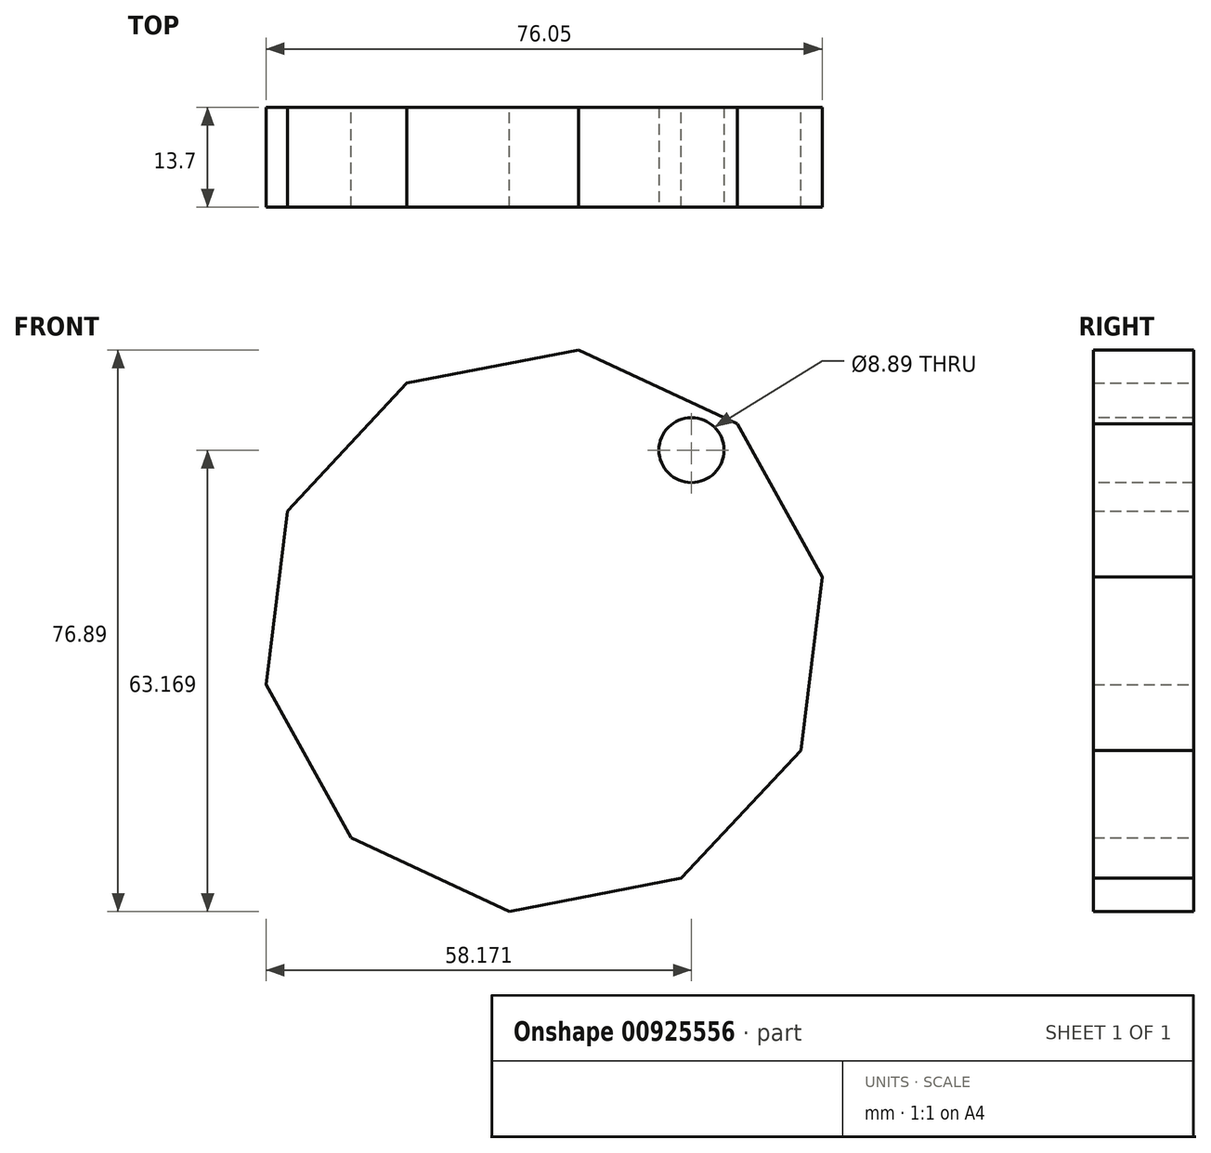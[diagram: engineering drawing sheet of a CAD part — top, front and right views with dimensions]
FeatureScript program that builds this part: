
annotation { "Feature Type Name" : "Feature", "Feature Type Description" : "" }
export const myFeature = defineFeature(function(context is Context, id is Id, definition is map)
    precondition{}
    {
        {
            var Q0;
            Q0=qCreatedBy(makeId("Front.planeOp"),FACE);
            var sketch = newSketch(context, id + "F0", { "sketchPlane" : qUnion([Q0])});
            skCircle(sketch, "E0.cCircle", {"center": v(-8.58, 14.77) * mm, "radius": 38.73 * mm, "construction": true});
            skLineSegment(sketch, "E0.0", {"start": v(10.19, -19.12) * mm, "end": v(-13.31, -23.68) * mm});
            skLineSegment(sketch, "E0.1", {"start": v(-13.31, -23.68) * mm, "end": v(-35, -13.56) * mm});
            skLineSegment(sketch, "E0.2", {"start": v(-35, -13.56) * mm, "end": v(-46.6, 7.38) * mm});
            skLineSegment(sketch, "E0.3", {"start": v(-46.6, 7.38) * mm, "end": v(-43.69, 31.14) * mm});
            skLineSegment(sketch, "E0.4", {"start": v(-43.69, 31.14) * mm, "end": v(-27.36, 48.65) * mm});
            skLineSegment(sketch, "E0.5", {"start": v(-27.36, 48.65) * mm, "end": v(-3.86, 53.2) * mm});
            skLineSegment(sketch, "E0.6", {"start": v(-3.86, 53.2) * mm, "end": v(17.84, 43.09) * mm});
            skLineSegment(sketch, "E0.7", {"start": v(17.84, 43.09) * mm, "end": v(29.44, 22.15) * mm});
            skLineSegment(sketch, "E0.8", {"start": v(29.44, 22.15) * mm, "end": v(26.52, -1.61) * mm});
            skLineSegment(sketch, "E0.9", {"start": v(26.52, -1.61) * mm, "end": v(10.19, -19.12) * mm});
            skSolve(sketch);
        }
        {
            var Q0;
            Q0 = qSketchRegion(id + "F0", true);
            extrude(context, id + "F1", {"entities" : qUnion([Q0]), "depth" : 13.7 * mm, "offsetDistance" : 25 * mm});
        }
        {
            var Q0;
            Q0=makeQuery(id+"F1.opExtrude","CAP_FACE",FACE,{"disambiguationData":[OSD([sQuery(id+"F0.wireOp",EDGE,"E0.0"),sQuery(id+"F0.wireOp",EDGE,"E0.1"),sQuery(id+"F0.wireOp",EDGE,"E0.2"),sQuery(id+"F0.wireOp",EDGE,"E0.3"),sQuery(id+"F0.wireOp",EDGE,"E0.4"),sQuery(id+"F0.wireOp",EDGE,"E0.5"),sQuery(id+"F0.wireOp",EDGE,"E0.6"),sQuery(id+"F0.wireOp",EDGE,"E0.7"),sQuery(id+"F0.wireOp",EDGE,"E0.8"),sQuery(id+"F0.wireOp",EDGE,"E0.9")])],"isStart":false});
            var sketch = newSketch(context, id + "F2", { "sketchPlane" : qUnion([Q0])});
            skCircle(sketch, "E1", {"center": v(11.56, 39.49) * mm, "radius": 4.44 * mm});
            skSolve(sketch);
        }
        {
            var Q0;
            Q0 = qSketchRegion(id + "F2", true);
            extrude(context, id + "F3", {"entities" : qUnion([Q0]), "operationType" : NewBodyOperationType.REMOVE, "oppositeDirection" : true, "depth" : 39.7 * mm, "offsetDistance" : 25 * mm});
        }
    });
